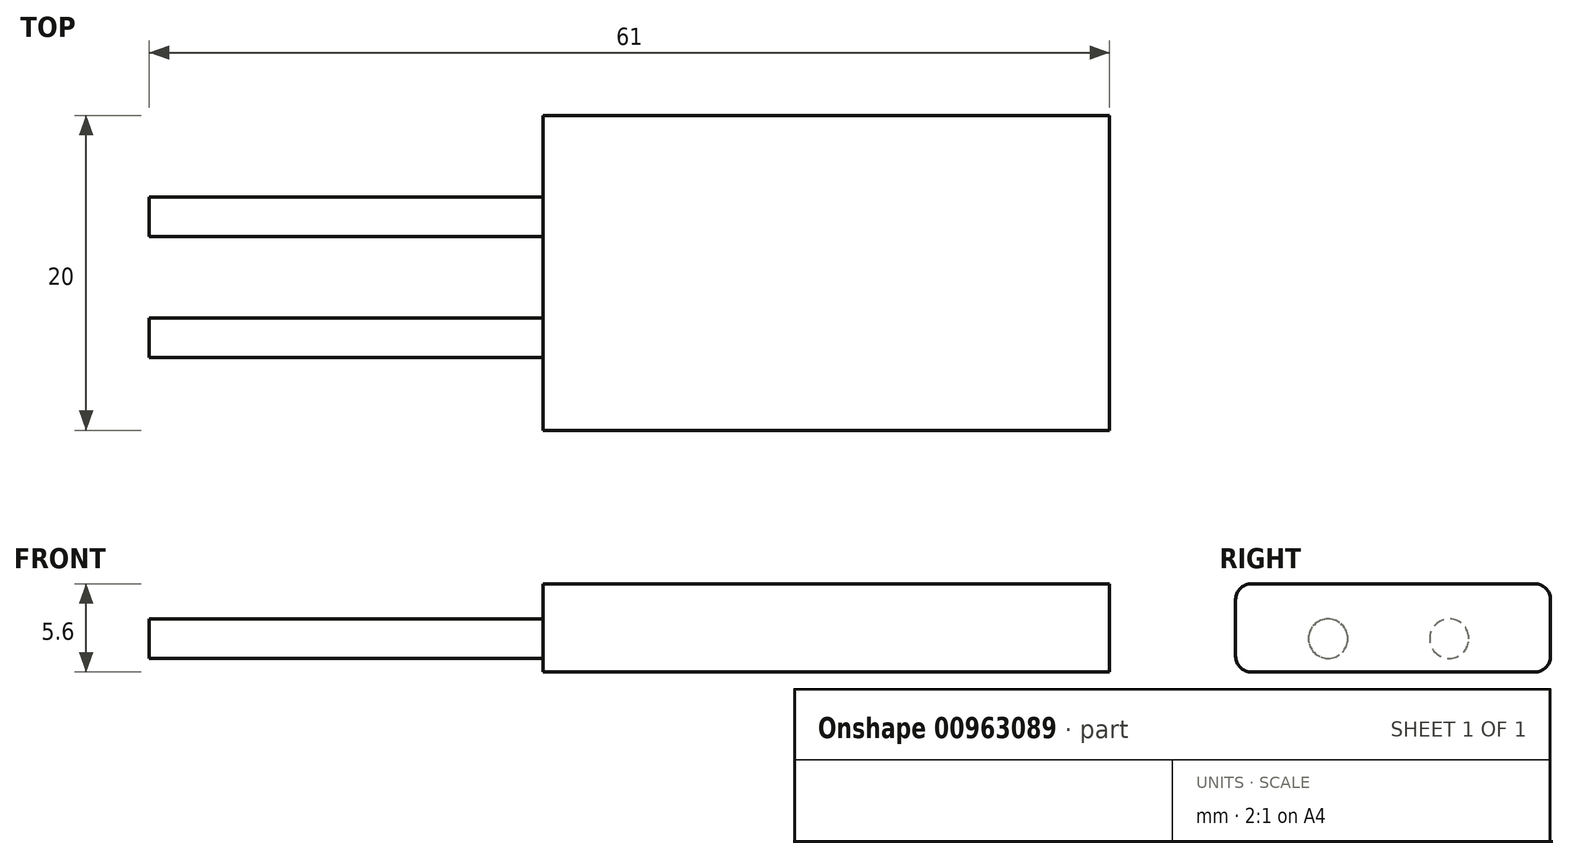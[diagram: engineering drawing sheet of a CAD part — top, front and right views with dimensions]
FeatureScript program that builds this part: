
annotation { "Feature Type Name" : "Feature", "Feature Type Description" : "" }
export const myFeature = defineFeature(function(context is Context, id is Id, definition is map)
    precondition{}
    {
        {
            var Q0;
            Q0=qCreatedBy(makeId("Top.planeOp"),FACE);
            var sketch = newSketch(context, id + "F0", { "sketchPlane" : qUnion([Q0])});
            skLineSegment(sketch, "E0.bottom", {"start": v(-18, 10) * mm, "end": v(18, 10) * mm});
            skLineSegment(sketch, "E0.top", {"start": v(-18, -10) * mm, "end": v(18, -10) * mm});
            skLineSegment(sketch, "E0.left", {"start": v(-18, 10) * mm, "end": v(-18, -10) * mm});
            skLineSegment(sketch, "E0.right", {"start": v(18, 10) * mm, "end": v(18, -10) * mm});
            skLineSegment(sketch, "E1", {"start": v(-18, 10) * mm, "end": v(18, -10) * mm, "construction": true});
            skSolve(sketch);
        }
        {
            var Q0;
            Q0 = qSketchRegion(id + "F0", true);
            extrude(context, id + "F1", {"entities" : qUnion([Q0]), "depth" : 5.6 * mm, "offsetDistance" : 25 * mm, "symmetric" : true});
        }
        {
            var Q0;
            Q0=makeQuery(id+"F1.opExtrude","SWEPT_FACE",FACE,{"disambiguationData":[OSD([sQuery(id+"F0.wireOp",EDGE,"E0.left")])]});
            var sketch = newSketch(context, id + "F2", { "sketchPlane" : qUnion([Q0])});
            skCircle(sketch, "E2", {"center": v(-3.57, -0.68) * mm, "radius": 1.25 * mm});
            skCircle(sketch, "E3", {"center": v(4.12, -0.68) * mm, "radius": 1.25 * mm});
            skSolve(sketch);
        }
        {
            var Q0;
            Q0 = qSketchRegion(id + "F2", true);
            extrude(context, id + "F3", {"entities" : qUnion([Q0]), "operationType" : NewBodyOperationType.ADD, "depth" : 25 * mm, "offsetDistance" : 25 * mm});
        }
        {
            var Q0;
            Q0=makeQuery(id+"F1.opExtrude","CAP_EDGE",EDGE,{"disambiguationData":[OSD([sQuery(id+"F0.wireOp",EDGE,"E0.top")])],"isStart":false});
            var Q1;
            Q1=makeQuery(id+"F1.opExtrude","CAP_EDGE",EDGE,{"disambiguationData":[OSD([sQuery(id+"F0.wireOp",EDGE,"E0.top")])],"isStart":true});
            var Q2;
            Q2=makeQuery(id+"F1.opExtrude","CAP_EDGE",EDGE,{"disambiguationData":[OSD([sQuery(id+"F0.wireOp",EDGE,"E0.bottom")])],"isStart":false});
            var Q3;
            Q3=makeQuery(id+"F1.opExtrude","CAP_EDGE",EDGE,{"disambiguationData":[OSD([sQuery(id+"F0.wireOp",EDGE,"E0.bottom")])],"isStart":true});
            fillet(context, id + "F4", {"entities" : qUnion([Q0, Q1, Q2, Q3]), "tangentPropagation" : true, "radius" : 1 * mm, "defaultsChanged" : true, "vertexSettings" : [], "allowEdgeOverflow" : false});
        }
    });
